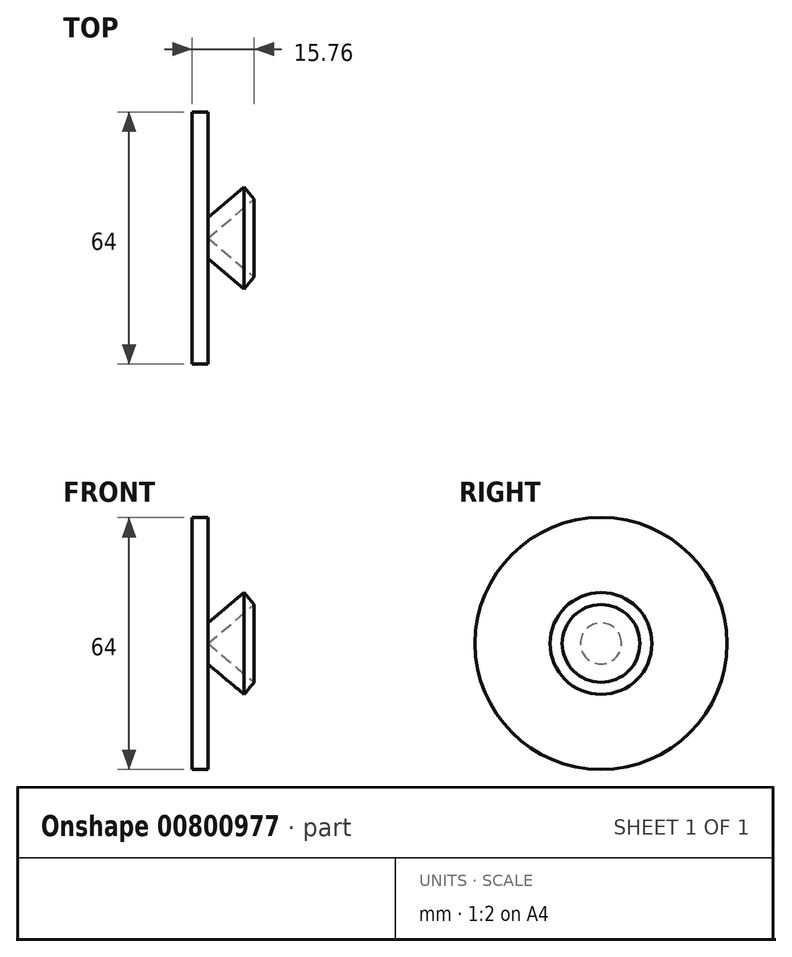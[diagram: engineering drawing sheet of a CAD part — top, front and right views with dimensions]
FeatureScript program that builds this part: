
annotation { "Feature Type Name" : "Feature", "Feature Type Description" : "" }
export const myFeature = defineFeature(function(context is Context, id is Id, definition is map)
    precondition{}
    {
        {
            var Q0;
            Q0=qCreatedBy(makeId("Top.planeOp"),FACE);
            var sketch = newSketch(context, id + "F0", { "sketchPlane" : qUnion([Q0])});
            skLineSegment(sketch, "E0", {"start": v(0, 0) * mm, "end": v(0, -32) * mm});
            skLineSegment(sketch, "E1", {"start": v(0, -32) * mm, "end": v(4, -32) * mm});
            skLineSegment(sketch, "E2", {"start": v(4, -32) * mm, "end": v(4, -5.22) * mm});
            skLineSegment(sketch, "E3", {"start": v(4, -5.22) * mm, "end": v(13.2, -12.94) * mm});
            skLineSegment(sketch, "E4", {"start": v(13.2, -12.94) * mm, "end": v(15.76, -9.87) * mm});
            skLineSegment(sketch, "E5", {"start": v(15.76, -9.87) * mm, "end": v(4, 0) * mm});
            skLineSegment(sketch, "E6", {"start": v(4, 0) * mm, "end": v(0, 0) * mm});
            skSolve(sketch);
        }
        {
            var Q0;
            Q0=makeQuery(id+"F0.imprint","IMPRINT",FACE,{"disambiguationData":[TD([[makeQuery(id+"F0.imprint","IMPRINT",EDGE,{"derivedFrom":sQuery(id+"F0.wireOp",EDGE,"E0")}),1.0]])]});
            var Q1;
            Q1=sQuery(id+"F0.wireOp",EDGE,"E6");
            revolve(context, id + "F1", {"surfaceOperationType" : NewSurfaceOperationType.NEW, "entities" : qUnion([Q0]), "axis" : qUnion([Q1]), "revolveType" : RevolveType.FULL});
        }
    });
